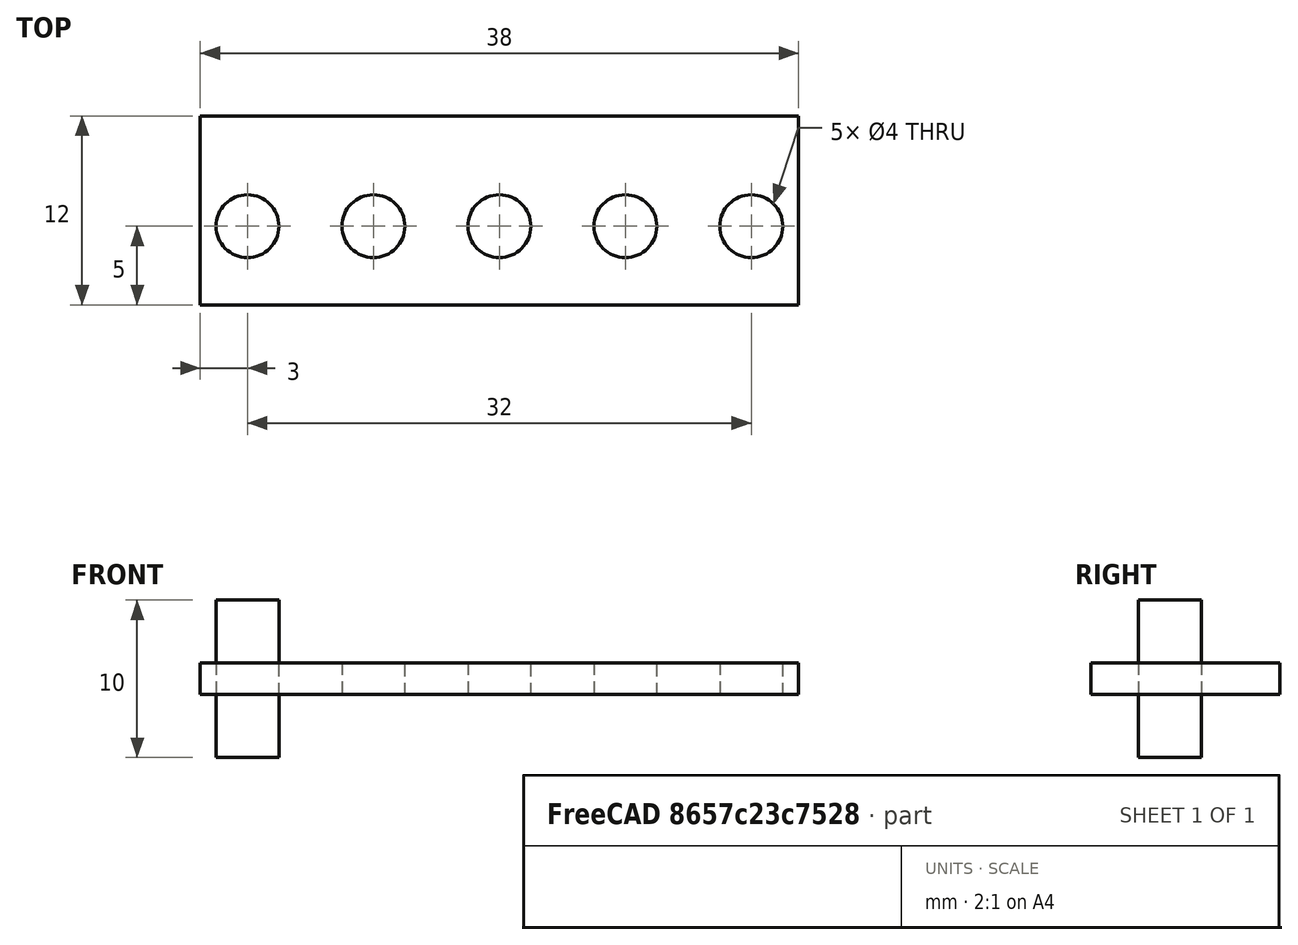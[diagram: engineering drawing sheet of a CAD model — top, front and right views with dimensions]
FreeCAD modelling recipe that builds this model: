
FCSTD DOCUMENT  (FreeCAD 0.20R29177 (Git))
Label: EjercicioVideo10
License: All rights reserved
LicenseURL: http://en.wikipedia.org/wiki/All_rights_reserved
objects: Part::Cylinder×1, Part::FeaturePython×1, Part::Box×1, Part::Cut×1
note: 3 computed .brp shape members not serialized (recipe doc carries the construction recipe); baked Part::Feature solids carry a one-line shape summary decoded from their .brp

FEATURE [Part::Cylinder] Cylinder  label="Cilindro"
  Angle = 360
  AttacherType = Attacher::AttachEngine3D
  FirstAngle = 0
  Height = 10
  Radius = 2
  SecondAngle = 0
FEATURE [Part::FeaturePython] Array  # Draft array (typed FeaturePython)
  AlwaysSyncPlacement = false
  Angle = 360
  ArrayType = 0
  Axis = (0,0,1)
  Base = -> Cylinder
  Center = (0,0,0)
  Count = 10
  ExpandArray = false
  Fuse = false
  IntervalAxis = (0,0,0)
  IntervalX = (8,0,0)
  IntervalY = (0,0,0)
  IntervalZ = (0,0,0)
  NumberCircles = 3
  NumberPolar = 5
  NumberX = 5
  NumberY = 2
  NumberZ = 1
  PlacementList = 10 placements: [(0,0,0),(0,0,0),(8,0,0),(8,0,0),(16,0,0),(16,0,0),(24,0,0),(24,0,0),(32,0,0),(32,0,0)]
  RadialDistance = 50
  ScaleList = (10) [(1,1,1),(1,1,1),(1,1,1),(1,1,1),(1,1,1),(1,1,1),(1,1,1),(1,1,1),(1,1,1),(1,1,1)]
  Symmetry = 1
  TangentialDistance = 25
FEATURE [Part::Box] Box  label="Cubo"
  AttacherType = Attacher::AttachEngine3D
  Height = 2
  Length = 38
  Placement = pos=(-3,-5,4) rot=(0,0,1;0rad)
  Width = 12
FEATURE [Part::Cut] Cut
  Base = -> Box
  Tool = -> Array
